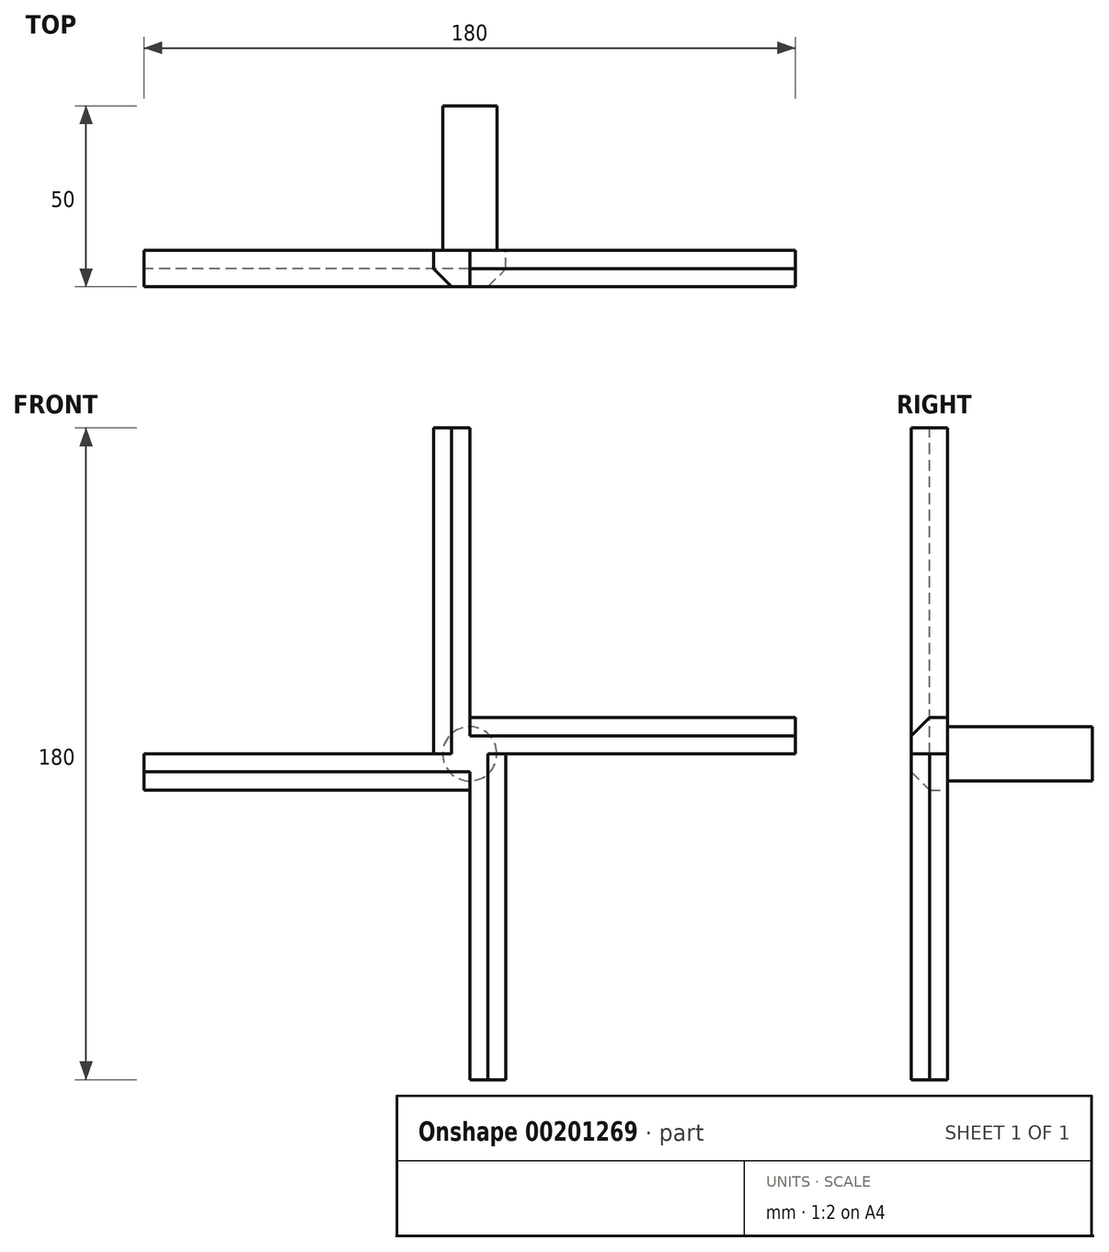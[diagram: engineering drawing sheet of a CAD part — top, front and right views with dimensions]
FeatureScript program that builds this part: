
annotation { "Feature Type Name" : "Feature", "Feature Type Description" : "" }
export const myFeature = defineFeature(function(context is Context, id is Id, definition is map)
    precondition{}
    {
        {
            var Q0;
            Q0=qCreatedBy(makeId("Front.planeOp"),FACE);
            var sketch = newSketch(context, id + "F0", { "sketchPlane" : qUnion([Q0])});
            skLineSegment(sketch, "E0.bottom", {"start": v(0, 0) * mm, "end": v(90, 0) * mm});
            skLineSegment(sketch, "E0.top", {"start": v(0, 10) * mm, "end": v(90, 10) * mm});
            skLineSegment(sketch, "E0.left", {"start": v(0, 0) * mm, "end": v(0, 10) * mm});
            skLineSegment(sketch, "E0.right", {"start": v(90, 0) * mm, "end": v(90, 10) * mm});
            skCircle(sketch, "E1", {"center": v(0, 0) * mm, "radius": 10 * mm});
            skLineSegment(sketch, "E2.1.1", {"start": v(0, 0) * mm, "end": v(0, 90) * mm});
            skLineSegment(sketch, "E2.1.2", {"start": v(-10, 0) * mm, "end": v(-10, 90) * mm});
            skLineSegment(sketch, "E2.1.3", {"start": v(0, 90) * mm, "end": v(-10, 90) * mm});
            skLineSegment(sketch, "E2.2.1", {"start": v(0, 0) * mm, "end": v(-90, 0) * mm});
            skLineSegment(sketch, "E2.2.2", {"start": v(0, -10) * mm, "end": v(-90, -10) * mm});
            skLineSegment(sketch, "E2.2.3", {"start": v(-90, 0) * mm, "end": v(-90, -10) * mm});
            skLineSegment(sketch, "E3.2.3.0", {"start": v(0, 0) * mm, "end": v(0, -90) * mm});
            skLineSegment(sketch, "E3.5.3.0", {"start": v(10, 0) * mm, "end": v(10, -90) * mm});
            skLineSegment(sketch, "E3.8.3.0", {"start": v(0, -90) * mm, "end": v(10, -90) * mm});
            skSolve(sketch);
        }
        {
            var Q0;
            {var subQ4=sQuery(id+"F0.wireOp",EDGE,"E2.1.2");Q0=makeQuery(id+"F0.imprint","IMPRINT",FACE,{"disambiguationData":[TD([[makeQuery(id+"F0.imprint","IMPRINT",EDGE,{"derivedFrom":subQ4}),-1.0]])]});}
            var Q1;
            {var subQ4=sQuery(id+"F0.wireOp",EDGE,"E2.2.2");Q1=makeQuery(id+"F0.imprint","IMPRINT",FACE,{"disambiguationData":[TD([[makeQuery(id+"F0.imprint","IMPRINT",EDGE,{"derivedFrom":subQ4}),-1.0]])]});}
            var Q2;
            {var subQ3=sQuery(id+"F0.wireOp",EDGE,"E3.5.3.0");Q2=makeQuery(id+"F0.imprint","IMPRINT",FACE,{"disambiguationData":[TD([[makeQuery(id+"F0.imprint","IMPRINT",EDGE,{"derivedFrom":subQ3}),-1.0]])]});}
            var Q3;
            {var subQ0=sQuery(id+"F0.wireOp",EDGE,"E2.1.1");var subQ3=sQuery(id+"F0.wireOp",EDGE,"E1");var subQ5=makeQuery(id+"F0.imprint","INTERSECT",VERTEX,{"derivedFrom":[sQuery(id+"F0.wireOp",EDGE,"E0.top"),subQ0,subQ3]});Q3=makeQuery(id+"F0.imprint","IMPRINT",FACE,{"disambiguationData":[TD([[makeQuery(id+"F0.imprint","IMPRINT",EDGE,{"disambiguationData":[TD([[subQ5,1.0]])],"derivedFrom":subQ3}),1.0]])]});}
            var Q4;
            {var subQ0=sQuery(id+"F0.wireOp",EDGE,"E3.2.3.0");var subQ3=sQuery(id+"F0.wireOp",EDGE,"E1");var subQ5=makeQuery(id+"F0.imprint","INTERSECT",VERTEX,{"derivedFrom":[sQuery(id+"F0.wireOp",EDGE,"E2.2.2"),subQ3,subQ0]});Q4=makeQuery(id+"F0.imprint","IMPRINT",FACE,{"disambiguationData":[TD([[makeQuery(id+"F0.imprint","IMPRINT",EDGE,{"disambiguationData":[TD([[subQ5,-1.0]])],"derivedFrom":subQ3}),1.0]])]});}
            var Q5;
            {var subQ1=sQuery(id+"F0.wireOp",EDGE,"E2.1.1");var subQ3=sQuery(id+"F0.wireOp",EDGE,"E1");var subQ4=makeQuery(id+"F0.imprint","INTERSECT",VERTEX,{"derivedFrom":[sQuery(id+"F0.wireOp",EDGE,"E0.top"),subQ1,subQ3]});Q5=makeQuery(id+"F0.imprint","IMPRINT",FACE,{"disambiguationData":[TD([[makeQuery(id+"F0.imprint","IMPRINT",EDGE,{"disambiguationData":[TD([[subQ4,-1.0]])],"derivedFrom":subQ3}),1.0]])]});}
            var Q6;
            {var subQ1=sQuery(id+"F0.wireOp",EDGE,"E2.2.1");var subQ3=sQuery(id+"F0.wireOp",EDGE,"E1");var subQ4=makeQuery(id+"F0.imprint","INTERSECT",VERTEX,{"derivedFrom":[sQuery(id+"F0.wireOp",EDGE,"E2.1.2"),subQ1,subQ3]});Q6=makeQuery(id+"F0.imprint","IMPRINT",FACE,{"disambiguationData":[TD([[makeQuery(id+"F0.imprint","IMPRINT",EDGE,{"disambiguationData":[TD([[subQ4,-1.0]])],"derivedFrom":subQ3}),1.0]])]});}
            var Q7;
            {var subQ4=sQuery(id+"F0.wireOp",EDGE,"E0.top");Q7=makeQuery(id+"F0.imprint","IMPRINT",FACE,{"disambiguationData":[TD([[makeQuery(id+"F0.imprint","IMPRINT",EDGE,{"derivedFrom":subQ4}),-1.0]])]});}
            extrude(context, id + "F1", {"entities" : qUnion([Q0, Q1, Q2, Q3, Q4, Q5, Q6, Q7]), "depth" : 10 * mm});
        }
        {
            var Q0;
            Q0=makeQuery(id+"F1.opExtrude","CAP_EDGE",EDGE,{"disambiguationData":[OSD([sQuery(id+"F0.wireOp",EDGE,"E2.1.2")])],"isStart":false});
            var Q1;
            Q1=makeQuery(id+"F1.opExtrude","CAP_EDGE",EDGE,{"disambiguationData":[OSD([sQuery(id+"F0.wireOp",EDGE,"E2.2.2")])],"isStart":false});
            var Q2;
            Q2=makeQuery(id+"F1.opExtrude","CAP_EDGE",EDGE,{"disambiguationData":[OSD([sQuery(id+"F0.wireOp",EDGE,"E3.5.3.0")])],"isStart":false});
            var Q3;
            Q3=makeQuery(id+"F1.opExtrude","CAP_EDGE",EDGE,{"disambiguationData":[OSD([sQuery(id+"F0.wireOp",EDGE,"E0.top")])],"isStart":false});
            chamfer(context, id + "F2", {"entities" : qUnion([Q0, Q1, Q2, Q3]), "width" : 5 * mm, "tangentPropagation" : true});
        }
        {
            var Q0;
            Q0=qCreatedBy(makeId("Front.planeOp"),FACE);
            var sketch = newSketch(context, id + "F3", { "sketchPlane" : qUnion([Q0])});
            skCircle(sketch, "E4", {"center": v(0, 0) * mm, "radius": 7.5 * mm});
            skSolve(sketch);
        }
        {
            var Q0;
            Q0=makeQuery(id+"F3.imprint","IMPRINT",FACE,{"disambiguationData":[TD([[makeQuery(id+"F3.imprint","IMPRINT",EDGE,{"derivedFrom":sQuery(id+"F3.wireOp",EDGE,"E4")}),1.0]])]});
            extrude(context, id + "F4", {"entities" : qUnion([Q0]), "operationType" : NewBodyOperationType.ADD, "oppositeDirection" : true, "depth" : 40 * mm});
        }
    });
